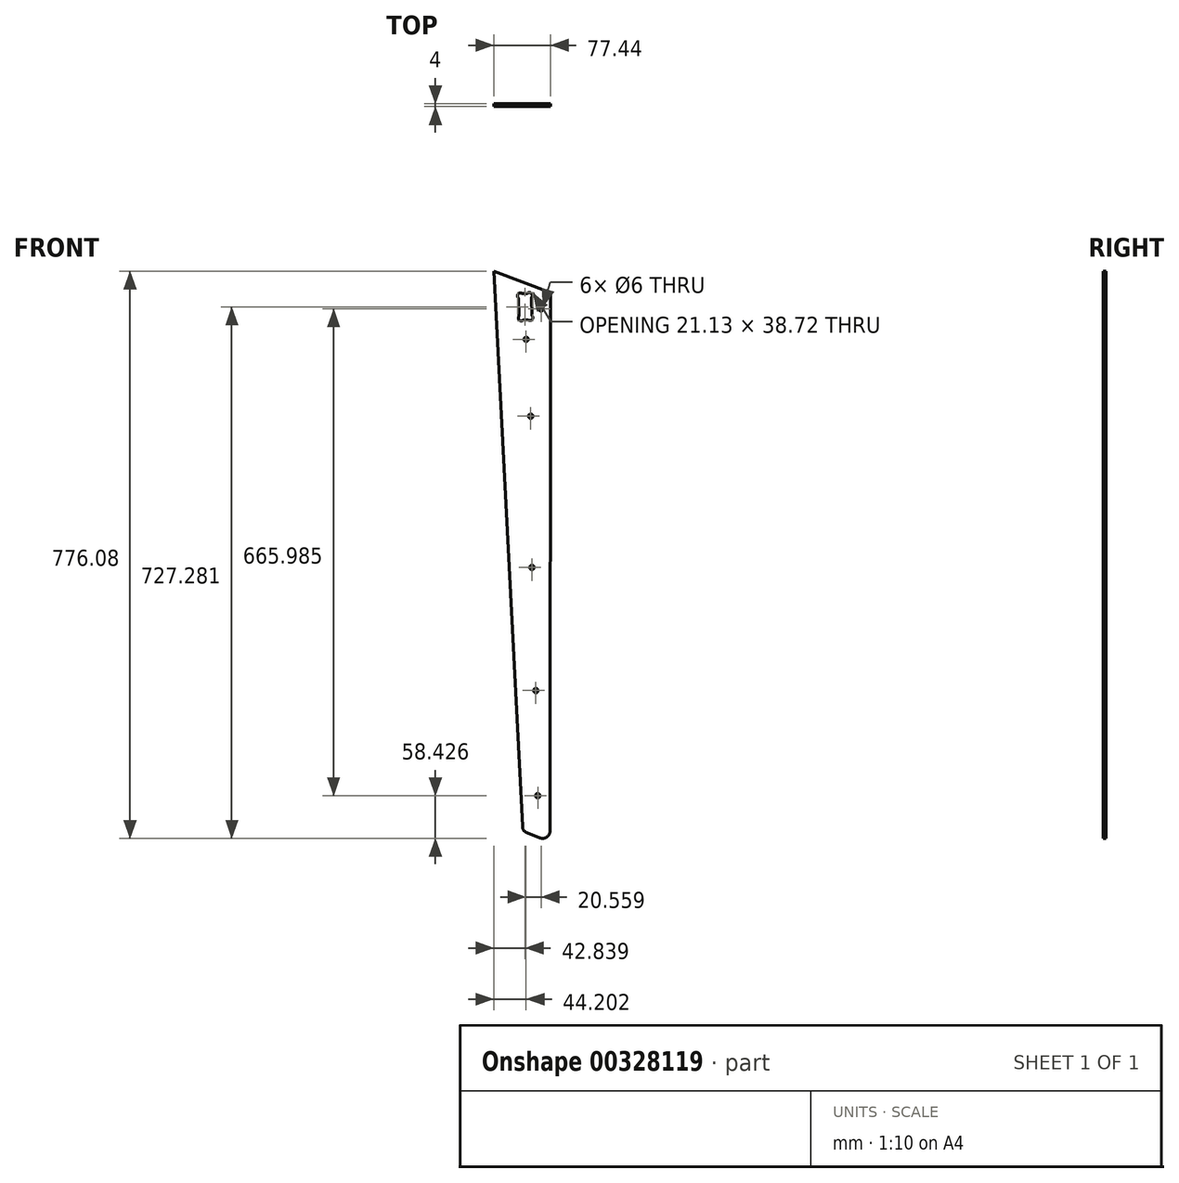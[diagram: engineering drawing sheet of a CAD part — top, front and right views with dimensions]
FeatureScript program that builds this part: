
annotation { "Feature Type Name" : "Feature", "Feature Type Description" : "" }
export const myFeature = defineFeature(function(context is Context, id is Id, definition is map)
    precondition{}
    {
        {
            var Q0;
            Q0=qCreatedBy(makeId("Front.planeOp"),FACE);
            var sketch = newSketch(context, id + "F0", { "sketchPlane" : qUnion([Q0])});
            skLineSegment(sketch, "E0", {"start": v(-41.3, 458.1) * mm, "end": v(-47.58, 457.9) * mm});
            skArc(sketch, "E1", {"start": v(-47.58, 457.9) * mm, "mid": v(-53.25, 457.74) * mm, "end": v(-53.38, 463.41) * mm});
            skLineSegment(sketch, "E2", {"start": v(-53.38, 463.41) * mm, "end": v(-54.4, 488) * mm});
            skArc(sketch, "E3", {"start": v(-54.4, 488) * mm, "mid": v(-54.64, 493.67) * mm, "end": v(-48.96, 493.87) * mm});
            skLineSegment(sketch, "E4", {"start": v(-48.96, 493.87) * mm, "end": v(-42.28, 494.1) * mm});
            skArc(sketch, "E5", {"start": v(-42.28, 494.1) * mm, "mid": v(-36.6, 494.26) * mm, "end": v(-36.49, 488.58) * mm});
            skLineSegment(sketch, "E6", {"start": v(-36.49, 488.58) * mm, "end": v(-35.87, 463.99) * mm});
            skArc(sketch, "E7", {"start": v(-35.87, 463.99) * mm, "mid": v(-35.62, 458.31) * mm, "end": v(-41.3, 458.1) * mm});
            skLineSegment(sketch, "E8", {"start": v(-24.74, -250.62) * mm, "end": v(-42.39, -243.89) * mm});
            skArc(sketch, "E9", {"start": v(-42.39, -243.89) * mm, "mid": v(-46.91, -240.43) * mm, "end": v(-48.81, -235.06) * mm});
            skLineSegment(sketch, "E10", {"start": v(-48.81, -235.06) * mm, "end": v(-87.97, 524.8) * mm});
            skLineSegment(sketch, "E11", {"start": v(-87.97, 524.8) * mm, "end": v(-10.53, 495.27) * mm});
            skLineSegment(sketch, "E12", {"start": v(-10.53, 495.27) * mm, "end": v(-11.17, -241.29) * mm});
            skArc(sketch, "E13", {"start": v(-11.17, -241.29) * mm, "mid": v(-15.5, -249.51) * mm, "end": v(-24.74, -250.62) * mm});
            skCircle(sketch, "E14", {"center": v(-37.61, 326.29) * mm, "radius": 3 * mm});
            skCircle(sketch, "E15", {"center": v(-35.82, 119.28) * mm, "radius": 3 * mm});
            skCircle(sketch, "E16", {"center": v(-23.2, 473.13) * mm, "radius": 3 * mm});
            skCircle(sketch, "E17", {"center": v(-30.54, -49.06) * mm, "radius": 3 * mm});
            skCircle(sketch, "E18", {"center": v(-27.88, -192.85) * mm, "radius": 3 * mm});
            skCircle(sketch, "E19", {"center": v(-43.77, 431.4) * mm, "radius": 3 * mm});
            skSolve(sketch);
        }
        {
            var Q0;
            Q0=makeQuery(id+"F0.imprint","IMPRINT",FACE,{"disambiguationData":[TD([[makeQuery(id+"F0.imprint","IMPRINT",EDGE,{"derivedFrom":sQuery(id+"F0.wireOp",EDGE,"E19")}),-1.0]])]});
            var Q1;
            Q1=makeQuery(id+"F0.imprint","IMPRINT",FACE,{"disambiguationData":[TD([[makeQuery(id+"F0.imprint","IMPRINT",EDGE,{"derivedFrom":sQuery(id+"F0.wireOp",EDGE,"E16")}),-1.0]])]});
            var Q2;
            Q2=makeQuery(id+"F0.imprint","IMPRINT",FACE,{"disambiguationData":[TD([[makeQuery(id+"F0.imprint","IMPRINT",EDGE,{"derivedFrom":sQuery(id+"F0.wireOp",EDGE,"E14")}),-1.0]])]});
            var Q3;
            Q3=makeQuery(id+"F0.imprint","IMPRINT",FACE,{"disambiguationData":[TD([[makeQuery(id+"F0.imprint","IMPRINT",EDGE,{"derivedFrom":sQuery(id+"F0.wireOp",EDGE,"E15")}),-1.0]])]});
            var Q4;
            Q4=makeQuery(id+"F0.imprint","IMPRINT",FACE,{"disambiguationData":[TD([[makeQuery(id+"F0.imprint","IMPRINT",EDGE,{"derivedFrom":sQuery(id+"F0.wireOp",EDGE,"E18")}),-1.0]])]});
            var Q5;
            Q5=makeQuery(id+"F0.imprint","IMPRINT",FACE,{"disambiguationData":[TD([[makeQuery(id+"F0.imprint","IMPRINT",EDGE,{"derivedFrom":sQuery(id+"F0.wireOp",EDGE,"E0")}),1.0]])]});
            var Q6;
            Q6=makeQuery(id+"F0.imprint","IMPRINT",FACE,{"disambiguationData":[TD([[makeQuery(id+"F0.imprint","IMPRINT",EDGE,{"derivedFrom":sQuery(id+"F0.wireOp",EDGE,"E17")}),-1.0]])]});
            extrude(context, id + "F1", {"entities" : qUnion([Q0, Q1, Q2, Q3, Q4, Q5, Q6]), "depth" : 18 * mm});
        }
        {
            var Q0;
            Q0=makeQuery(id+"F0.imprint","IMPRINT",FACE,{"disambiguationData":[TD([[makeQuery(id+"F0.imprint","IMPRINT",EDGE,{"derivedFrom":sQuery(id+"F0.wireOp",EDGE,"E19")}),-1.0]])]});
            var Q1;
            Q1=makeQuery(id+"F0.imprint","IMPRINT",FACE,{"disambiguationData":[TD([[makeQuery(id+"F0.imprint","IMPRINT",EDGE,{"derivedFrom":sQuery(id+"F0.wireOp",EDGE,"E16")}),-1.0]])]});
            var Q2;
            Q2=makeQuery(id+"F0.imprint","IMPRINT",FACE,{"disambiguationData":[TD([[makeQuery(id+"F0.imprint","IMPRINT",EDGE,{"derivedFrom":sQuery(id+"F0.wireOp",EDGE,"E14")}),-1.0]])]});
            var Q3;
            Q3=makeQuery(id+"F0.imprint","IMPRINT",FACE,{"disambiguationData":[TD([[makeQuery(id+"F0.imprint","IMPRINT",EDGE,{"derivedFrom":sQuery(id+"F0.wireOp",EDGE,"E15")}),-1.0]])]});
            var Q4;
            Q4=makeQuery(id+"F0.imprint","IMPRINT",FACE,{"disambiguationData":[TD([[makeQuery(id+"F0.imprint","IMPRINT",EDGE,{"derivedFrom":sQuery(id+"F0.wireOp",EDGE,"E18")}),-1.0]])]});
            var Q5;
            Q5=makeQuery(id+"F0.imprint","IMPRINT",FACE,{"disambiguationData":[TD([[makeQuery(id+"F0.imprint","IMPRINT",EDGE,{"derivedFrom":sQuery(id+"F0.wireOp",EDGE,"E17")}),-1.0]])]});
            extrude(context, id + "F2", {"entities" : qUnion([Q0, Q1, Q2, Q3, Q4, Q5]), "operationType" : NewBodyOperationType.REMOVE, "depth" : 14 * mm});
        }
    });
